# Revit family: Juxta_Stools_Star_Base_Models_44140_44141_44150_44151
name_source: partatom
category: Furniture
units: mm (PartAtom-declared; Revit-internal decimal feet)

## family parameters
Always vertical = Yes
Cut with Voids When Loaded = No
OmniClass Number = 23.40.70.14.64.11
OmniClass Title = Office Furniture
Room Calculation Point = No
Shared = No
Work Plane-Based = No

## types (4) — shared parameters
Assembly Code = E2020200
Catalog = JUXTA
Manufacturer = Keilhauer, Corp.
Product Documentation Link = http://www.keilhauer.com
URL = http://www.keilhauer.com
zero-valued in all types: Default Elevation

## per-type parameters (varying)
| type | Description | Five Star | Five Star w/o Tablet | Five Tablet | Four Star | Four Star w/o Tablet | Four Tablet | Height | Model | Tablet | Without Tablet |
| Stool with 4 Star Base | Juxta Stool with 4 Star Base | No | No | No | Yes | Yes | No | 13.77 " | 44140 | No | Yes |
| Stool with 4 Star Base with Tablet | Juxta Stool 4 Star Base with Tablet | No | No | No | Yes | No | Yes | 13.77 " | 44141 | Yes | No |
| Stool with 5 Star Base | Juxta Stool with 5 Star Base | Yes | Yes | No | No | No | No | 14.62 " | 44150 | No | Yes |
| Stool 5 Star Base with Tablet | Juxta Stool 5 Star Base with Tablet | Yes | No | Yes | No | No | No | 14.62 " | 44151 | Yes | No |

## geometry (parser evidence)
native form markers: Sweep x3
no freeform markers — native parametric forms only
